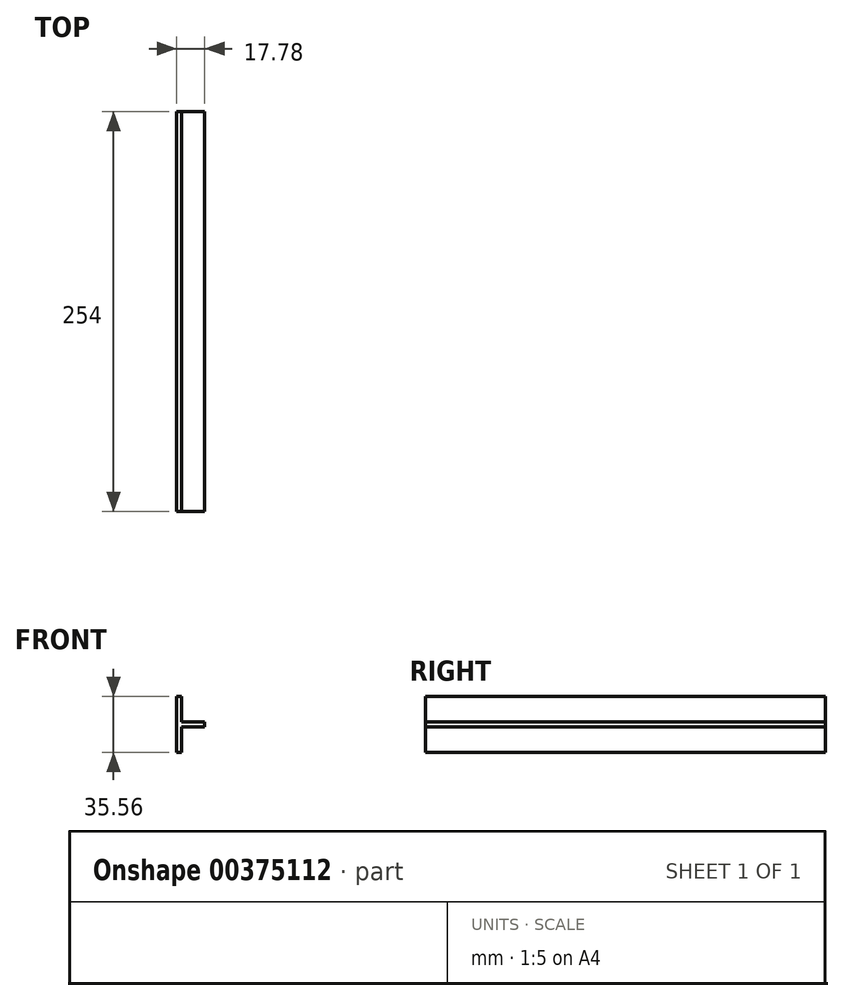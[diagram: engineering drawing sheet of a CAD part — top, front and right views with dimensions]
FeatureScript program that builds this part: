
annotation { "Feature Type Name" : "Feature", "Feature Type Description" : "" }
export const myFeature = defineFeature(function(context is Context, id is Id, definition is map)
    precondition{}
    {
        {
            var Q0;
            Q0=qCreatedBy(makeId("Front.planeOp"),FACE);
            var sketch = newSketch(context, id + "F0", { "sketchPlane" : qUnion([Q0])});
            skLineSegment(sketch, "E0", {"start": v(0, 0) * mm, "end": v(3.18, 0) * mm});
            skLineSegment(sketch, "E1", {"start": v(3.18, 0) * mm, "end": v(3.17, 16.2) * mm});
            skLineSegment(sketch, "E2", {"start": v(3.17, 16.2) * mm, "end": v(17.78, 16.2) * mm});
            skLineSegment(sketch, "E3", {"start": v(17.78, 16.2) * mm, "end": v(17.78, 19.37) * mm});
            skLineSegment(sketch, "E4", {"start": v(17.78, 19.37) * mm, "end": v(3.17, 19.37) * mm});
            skLineSegment(sketch, "E5", {"start": v(3.17, 19.37) * mm, "end": v(3.17, 35.56) * mm});
            skLineSegment(sketch, "E6", {"start": v(3.17, 35.56) * mm, "end": v(0, 35.56) * mm});
            skLineSegment(sketch, "E7", {"start": v(0, 35.56) * mm, "end": v(0, 0) * mm});
            skLineSegment(sketch, "E8", {"start": v(0, 17.78) * mm, "end": v(-5.54, 17.78) * mm});
            skSolve(sketch);
        }
        {
            var Q0;
            {var subQ0=sQuery(id+"F0.wireOp",EDGE,"E0");Q0=makeQuery(id+"F0.imprint","IMPRINT",FACE,{"disambiguationData":[TD([[makeQuery(id+"F0.imprint","IMPRINT",EDGE,{"derivedFrom":subQ0}),1.0]])]});}
            extrude(context, id + "F1", {"entities" : qUnion([Q0]), "oppositeDirection" : true, "depth" : 254 * mm});
        }
    });
